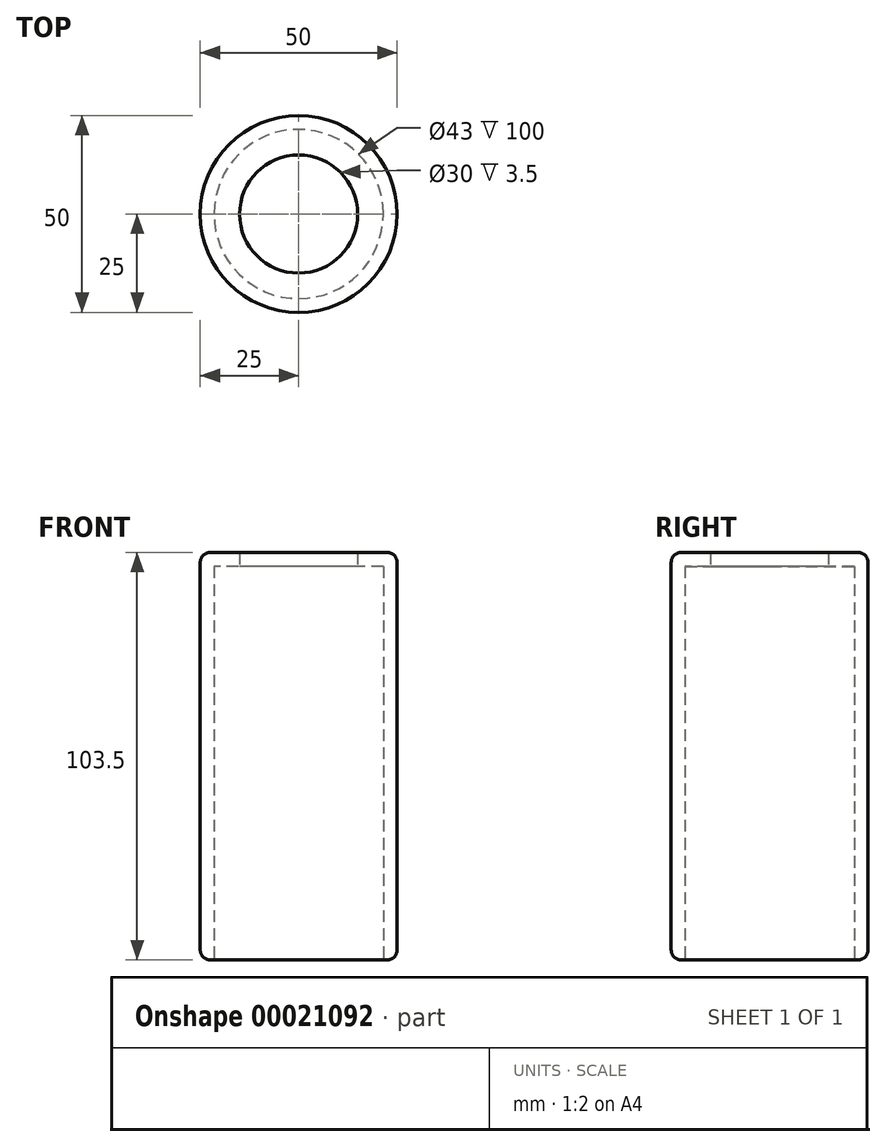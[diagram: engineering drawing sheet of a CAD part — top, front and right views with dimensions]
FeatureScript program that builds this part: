
annotation { "Feature Type Name" : "Feature", "Feature Type Description" : "" }
export const myFeature = defineFeature(function(context is Context, id is Id, definition is map)
    precondition{}
    {
        {
            var Q0;
            Q0=qCreatedBy(makeId("Top.planeOp"),FACE);
            var sketch = newSketch(context, id + "F0", { "sketchPlane" : qUnion([Q0])});
            skCircle(sketch, "E0", {"center": v(0, 0) * mm, "radius": 25 * mm});
            skCircle(sketch, "E1", {"center": v(0, 0) * mm, "radius": 21.5 * mm});
            skSolve(sketch);
        }
        {
            var Q0;
            Q0 = qSketchRegion(id + "F0", true);
            extrude(context, id + "F1", {"entities" : qUnion([Q0]), "depth" : 100 * mm});
        }
        {
            var Q0;
            Q0=makeQuery(id+"F1.opExtrude","CAP_FACE",FACE,{"disambiguationData":[OSD([sQuery(id+"F0.wireOp",EDGE,"E0"),sQuery(id+"F0.wireOp",EDGE,"E1")])],"isStart":false});
            var sketch = newSketch(context, id + "F2", { "sketchPlane" : qUnion([Q0])});
            skCircle(sketch, "E2", {"center": v(0, 0) * mm, "radius": 25 * mm});
            skCircle(sketch, "E3", {"center": v(0, 0) * mm, "radius": 15 * mm});
            skSolve(sketch);
        }
        {
            var Q0;
            Q0 = qSketchRegion(id + "F2", true);
            extrude(context, id + "F3", {"entities" : qUnion([Q0]), "operationType" : NewBodyOperationType.ADD, "depth" : 3.5 * mm});
        }
        {
            var Q0;
            Q0=makeQuery(id+"F3.opExtrude","CAP_EDGE",EDGE,{"disambiguationData":[OSD([sQuery(id+"F2.wireOp",EDGE,"E2")])],"isStart":false});
            var Q1;
            Q1=makeQuery(id+"F1.opExtrude","CAP_EDGE",EDGE,{"disambiguationData":[OSD([sQuery(id+"F0.wireOp",EDGE,"E0")])],"isStart":true});
            fillet(context, id + "F4", {"entities" : qUnion([Q0, Q1]), "radius" : 2.5 * mm, "tangentPropagation" : true, "allowEdgeOverflow" : false});
        }
    });
